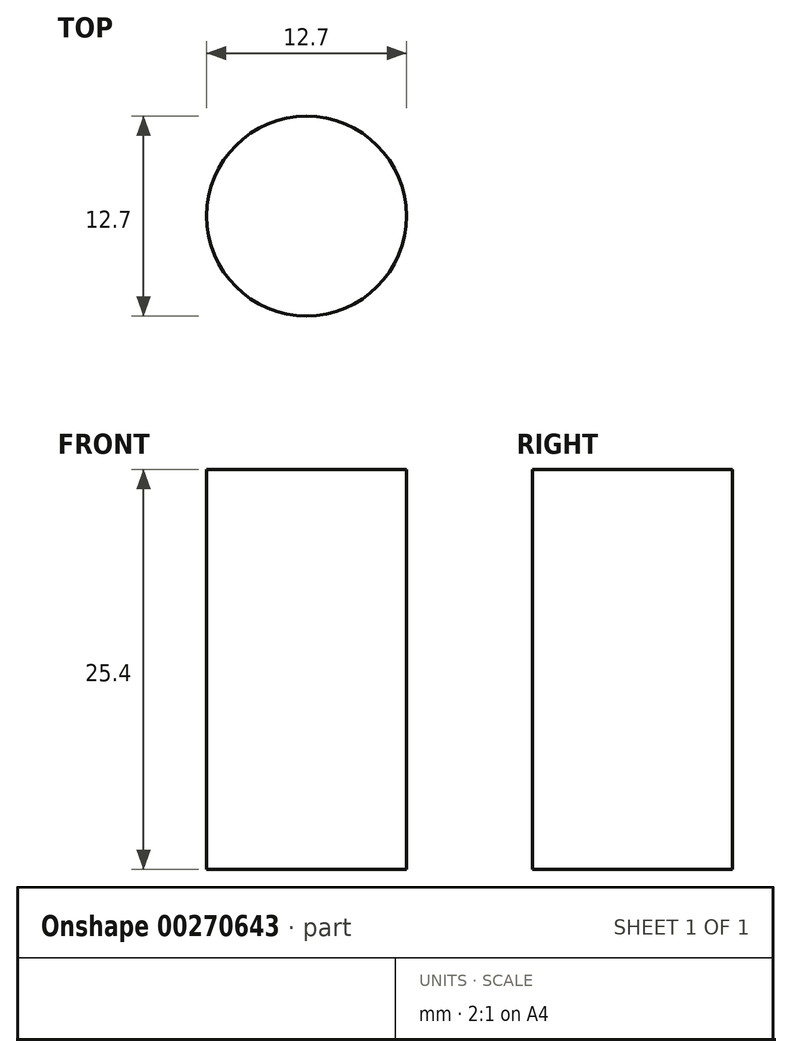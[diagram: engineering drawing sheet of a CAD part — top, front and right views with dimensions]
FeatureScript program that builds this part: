
annotation { "Feature Type Name" : "Feature", "Feature Type Description" : "" }
export const myFeature = defineFeature(function(context is Context, id is Id, definition is map)
    precondition{}
    {
        {
            var Q0;
            Q0=qCreatedBy(makeId("Top.planeOp"),FACE);
            var sketch = newSketch(context, id + "F0", { "sketchPlane" : qUnion([Q0])});
            skCircle(sketch, "E0", {"center": v(0, 0) * mm, "radius": 6.35 * mm});
            skSolve(sketch);
        }
        {
            var Q0;
            Q0 = qSketchRegion(id + "F0", true);
            extrude(context, id + "F1", {"entities" : qUnion([Q0]), "depth" : 25.4 * mm});
        }
    });
